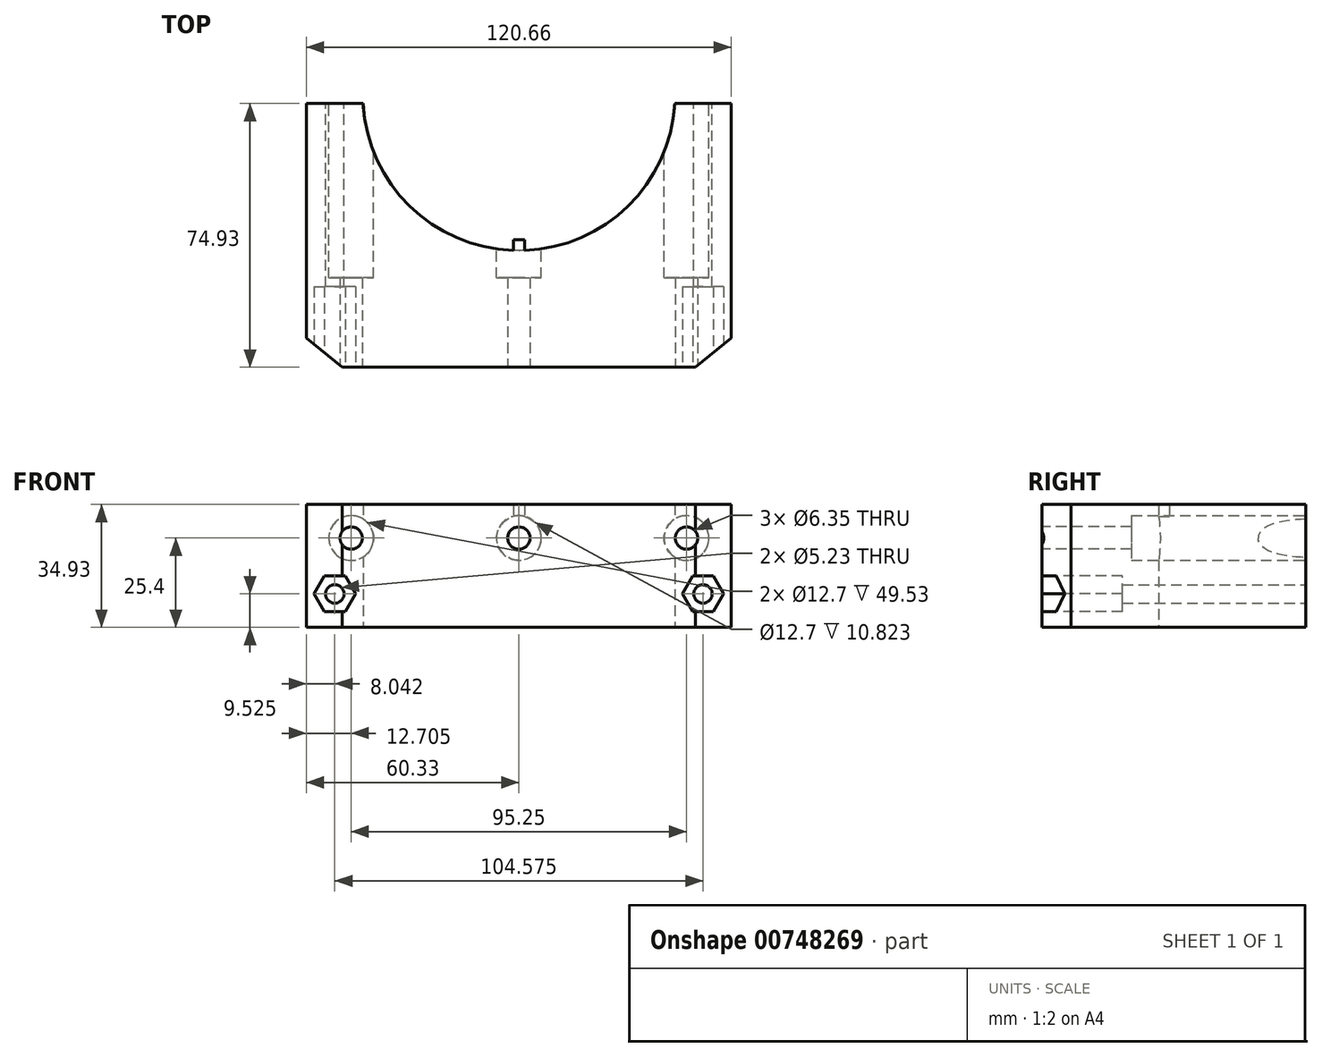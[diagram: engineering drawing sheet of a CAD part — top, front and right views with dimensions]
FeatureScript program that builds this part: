
annotation { "Feature Type Name" : "Feature", "Feature Type Description" : "" }
export const myFeature = defineFeature(function(context is Context, id is Id, definition is map)
    precondition{}
    {
        {
            var Q0;
            Q0=qCreatedBy(makeId("Top.planeOp"),FACE);
            var sketch = newSketch(context, id + "F0", { "sketchPlane" : qUnion([Q0])});
            skCircle(sketch, "E0", {"center": v(0, 0) * mm, "radius": 44.32 * mm, "construction": true});
            skLineSegment(sketch, "E1.bottom", {"start": v(60.32, -77.47) * mm, "end": v(-60.33, -77.47) * mm, "construction": true});
            skLineSegment(sketch, "E1.top", {"start": v(60.33, 77.47) * mm, "end": v(-60.32, 77.47) * mm, "construction": true});
            skLineSegment(sketch, "E1.left", {"start": v(60.33, -77.47) * mm, "end": v(60.33, 77.47) * mm, "construction": true});
            skLineSegment(sketch, "E1.right", {"start": v(-60.33, -77.47) * mm, "end": v(-60.32, 77.47) * mm, "construction": true});
            skLineSegment(sketch, "E2", {"start": v(-60.33, 0) * mm, "end": v(60.32, 0) * mm, "construction": true});
            skLineSegment(sketch, "E3.0", {"start": v(-60.33, -2.54) * mm, "end": v(60.32, -2.54) * mm, "construction": true});
            skLineSegment(sketch, "E4", {"start": v(-44.25, -2.54) * mm, "end": v(-60.33, -2.54) * mm});
            skLineSegment(sketch, "E5", {"start": v(-60.33, -2.54) * mm, "end": v(-60.33, -69.19) * mm});
            skLineSegment(sketch, "E6", {"start": v(-50.17, -77.47) * mm, "end": v(50.16, -77.47) * mm});
            skLineSegment(sketch, "E7", {"start": v(60.32, -69.19) * mm, "end": v(60.32, -2.54) * mm});
            skLineSegment(sketch, "E8", {"start": v(60.32, -2.54) * mm, "end": v(44.25, -2.54) * mm});
            skLineSegment(sketch, "E9", {"start": v(0, -44.32) * mm, "end": v(0, -77.47) * mm, "construction": true});
            skLineSegment(sketch, "E10.0", {"start": v(-1.59, -43.72) * mm, "end": v(-1.59, -60.32) * mm, "construction": true});
            skLineSegment(sketch, "E11.0", {"start": v(1.59, -43.93) * mm, "end": v(1.59, -60.33) * mm, "construction": true});
            skArc(sketch, "E12", {"start": v(1.59, -44.3) * mm, "mid": v(31, -31.68) * mm, "end": v(44.25, -2.54) * mm});
            skArc(sketch, "E13", {"start": v(-44.25, -2.54) * mm, "mid": v(-31, -31.68) * mm, "end": v(-1.59, -44.3) * mm});
            skLineSegment(sketch, "E14", {"start": v(-1.59, -44.3) * mm, "end": v(-1.59, -41.25) * mm});
            skLineSegment(sketch, "E15", {"start": v(1.59, -44.3) * mm, "end": v(1.59, -41.25) * mm});
            skLineSegment(sketch, "E16", {"start": v(-1.59, -41.25) * mm, "end": v(1.59, -41.25) * mm});
            skLineSegment(sketch, "E17.0", {"start": v(-50.17, -2.54) * mm, "end": v(-50.17, -77.47) * mm, "construction": true});
            skLineSegment(sketch, "E18.0", {"start": v(50.16, -77.47) * mm, "end": v(50.16, -2.54) * mm, "construction": true});
            skLineSegment(sketch, "E19.0", {"start": v(-60.33, -69.19) * mm, "end": v(60.32, -69.19) * mm, "construction": true});
            skLineSegment(sketch, "E20", {"start": v(-60.33, -69.19) * mm, "end": v(-50.17, -77.47) * mm});
            skLineSegment(sketch, "E21", {"start": v(60.32, -69.19) * mm, "end": v(50.16, -77.47) * mm});
            skSolve(sketch);
        }
        {
            var Q0;
            Q0 = qSketchRegion(id + "F0", true);
            extrude(context, id + "F1", {"entities" : qUnion([Q0]), "depth" : 34.92 * mm, "offsetDistance" : 25.4 * mm});
        }
        {
            var Q0;
            Q0=makeQuery(id+"F1.opExtrude","SWEPT_FACE",FACE,{"disambiguationData":[OSD([sQuery(id+"F0.wireOp",EDGE,"E8")])]});
            var sketch = newSketch(context, id + "F2", { "sketchPlane" : qUnion([Q0])});
            skLineSegment(sketch, "E22", {"start": v(-52.29, 34.93) * mm, "end": v(-52.29, 0) * mm, "construction": true});
            skLineSegment(sketch, "E23", {"start": v(-60.32, 9.53) * mm, "end": v(-44.25, 9.53) * mm, "construction": true});
            skCircle(sketch, "E24", {"center": v(-52.29, 9.53) * mm, "radius": 2.62 * mm});
            skSolve(sketch);
        }
        {
            var Q0;
            Q0 = qSketchRegion(id + "F2", true);
            extrude(context, id + "F3", {"entities" : qUnion([Q0]), "operationType" : NewBodyOperationType.REMOVE, "endBound" : BoundingType.THROUGH_ALL, "oppositeDirection" : true, "depth" : 25.4 * mm, "offsetDistance" : 25.4 * mm});
        }
        {
            var Q0;
            Q0=makeQuery(id+"F1.opExtrude","SWEPT_FACE",FACE,{"disambiguationData":[OSD([sQuery(id+"F0.wireOp",EDGE,"E4")])]});
            var sketch = newSketch(context, id + "F4", { "sketchPlane" : qUnion([Q0])});
            skLineSegment(sketch, "E25", {"start": v(52.29, 34.93) * mm, "end": v(52.29, 0) * mm, "construction": true});
            skLineSegment(sketch, "E26", {"start": v(44.25, 9.53) * mm, "end": v(60.33, 9.53) * mm, "construction": true});
            skCircle(sketch, "E27", {"center": v(52.29, 9.53) * mm, "radius": 2.62 * mm});
            skSolve(sketch);
        }
        {
            var Q0;
            Q0 = qSketchRegion(id + "F4", true);
            extrude(context, id + "F5", {"entities" : qUnion([Q0]), "operationType" : NewBodyOperationType.REMOVE, "endBound" : BoundingType.THROUGH_ALL, "oppositeDirection" : true, "depth" : 25.4 * mm, "offsetDistance" : 25.4 * mm});
        }
        {
            var Q0;
            Q0=makeQuery(id+"F1.opExtrude","SWEPT_FACE",FACE,{"disambiguationData":[OSD([sQuery(id+"F0.wireOp",EDGE,"E6")])]});
            var sketch = newSketch(context, id + "F6", { "sketchPlane" : qUnion([Q0])});
            skLineSegment(sketch, "E28", {"start": v(-60.33, 25.4) * mm, "end": v(60.33, 25.4) * mm, "construction": true});
            skCircle(sketch, "E29", {"center": v(-47.63, 25.4) * mm, "radius": 3.18 * mm});
            skCircle(sketch, "E30", {"center": v(47.63, 25.4) * mm, "radius": 3.18 * mm});
            skCircle(sketch, "E31", {"center": v(0, 25.4) * mm, "radius": 3.18 * mm});
            skLineSegment(sketch, "E32", {"start": v(0, 0) * mm, "end": v(0, 34.93) * mm, "construction": true});
            skSolve(sketch);
        }
        {
            var Q0;
            Q0 = qSketchRegion(id + "F6", true);
            extrude(context, id + "F7", {"entities" : qUnion([Q0]), "operationType" : NewBodyOperationType.REMOVE, "endBound" : BoundingType.THROUGH_ALL, "oppositeDirection" : true, "depth" : 25.4 * mm, "offsetDistance" : 25.4 * mm});
        }
        {
            var Q0;
            Q0=makeQuery(id+"F1.opExtrude","SWEPT_FACE",FACE,{"disambiguationData":[OSD([sQuery(id+"F0.wireOp",EDGE,"E8")])]});
            var sketch = newSketch(context, id + "F8", { "sketchPlane" : qUnion([Q0])});
            skCircle(sketch, "E33", {"center": v(-47.63, 25.4) * mm, "radius": 6.35 * mm});
            skLineSegment(sketch, "E34", {"start": v(-47.63, 25.4) * mm, "end": v(47.63, 25.4) * mm, "construction": true});
            skCircle(sketch, "E35", {"center": v(0, 25.4) * mm, "radius": 6.35 * mm});
            skCircle(sketch, "E36", {"center": v(47.63, 25.4) * mm, "radius": 6.35 * mm});
            skSolve(sketch);
        }
        {
            var Q0;
            Q0 = qSketchRegion(id + "F8", true);
            extrude(context, id + "F9", {"entities" : qUnion([Q0]), "operationType" : NewBodyOperationType.REMOVE, "oppositeDirection" : true, "depth" : 49.53 * mm, "offsetDistance" : 25.4 * mm});
        }
        {
            var Q0;
            Q0=makeQuery(id+"F1.opExtrude","SWEPT_FACE",FACE,{"disambiguationData":[OSD([sQuery(id+"F0.wireOp",EDGE,"E6")])]});
            var sketch = newSketch(context, id + "F10", { "sketchPlane" : qUnion([Q0])});
            skCircle(sketch, "E37.cCircle", {"center": v(-52.29, 9.53) * mm, "radius": 5.08 * mm, "construction": true});
            skLineSegment(sketch, "E37.0", {"start": v(-46.42, 9.52) * mm, "end": v(-49.35, 4.45) * mm});
            skLineSegment(sketch, "E37.1", {"start": v(-49.35, 4.45) * mm, "end": v(-55.22, 4.45) * mm});
            skLineSegment(sketch, "E37.2", {"start": v(-55.22, 4.45) * mm, "end": v(-58.15, 9.53) * mm});
            skLineSegment(sketch, "E37.3", {"start": v(-58.15, 9.53) * mm, "end": v(-55.22, 14.6) * mm});
            skLineSegment(sketch, "E37.4", {"start": v(-55.22, 14.6) * mm, "end": v(-49.35, 14.6) * mm});
            skLineSegment(sketch, "E37.5", {"start": v(-49.35, 14.6) * mm, "end": v(-46.42, 9.52) * mm});
            skPoint(sketch, "E37.0.midPoint", {"position": v(-47.89, 6.98) * mm});
            skLineSegment(sketch, "E38", {"start": v(-52.29, 9.53) * mm, "end": v(52.29, 9.53) * mm, "construction": true});
            skCircle(sketch, "E39.cCircle", {"center": v(52.29, 9.53) * mm, "radius": 5.08 * mm, "construction": true});
            skLineSegment(sketch, "E39.0", {"start": v(46.42, 9.53) * mm, "end": v(49.35, 14.6) * mm});
            skLineSegment(sketch, "E39.1", {"start": v(49.35, 14.6) * mm, "end": v(55.22, 14.6) * mm});
            skLineSegment(sketch, "E39.2", {"start": v(55.22, 14.6) * mm, "end": v(58.15, 9.52) * mm});
            skLineSegment(sketch, "E39.3", {"start": v(58.15, 9.53) * mm, "end": v(55.22, 4.45) * mm});
            skLineSegment(sketch, "E39.4", {"start": v(55.22, 4.45) * mm, "end": v(49.35, 4.45) * mm});
            skLineSegment(sketch, "E39.5", {"start": v(49.35, 4.44) * mm, "end": v(46.42, 9.53) * mm});
            skPoint(sketch, "E39.0.midPoint", {"position": v(47.89, 12.07) * mm});
            skLineSegment(sketch, "E40.1", {"start": v(-46.42, 9.53) * mm, "end": v(-49.35, 4.45) * mm});
            skLineSegment(sketch, "E40.3", {"start": v(-55.22, 4.44) * mm, "end": v(-58.15, 9.53) * mm});
            skPoint(sketch, "E40.0.midPoint", {"position": v(-47.89, 12.07) * mm});
            skLineSegment(sketch, "E41.2", {"start": v(49.35, 4.45) * mm, "end": v(46.42, 9.53) * mm});
            skLineSegment(sketch, "E41.5", {"start": v(55.22, 14.6) * mm, "end": v(58.15, 9.53) * mm});
            skPoint(sketch, "E41.0.midPoint", {"position": v(56.69, 6.98) * mm});
            skSolve(sketch);
        }
        {
            var Q0;
            Q0 = qSketchRegion(id + "F10", true);
            extrude(context, id + "F11", {"entities" : qUnion([Q0]), "operationType" : NewBodyOperationType.REMOVE, "oppositeDirection" : true, "depth" : 22.86 * mm, "offsetDistance" : 25.4 * mm});
        }
        {
            var Q0;
            Q0=makeQuery(id+"F1.opExtrude","CAP_FACE",FACE,{"disambiguationData":[OSD([sQuery(id+"F0.wireOp",EDGE,"E4"),sQuery(id+"F0.wireOp",EDGE,"E5"),sQuery(id+"F0.wireOp",EDGE,"E6"),sQuery(id+"F0.wireOp",EDGE,"E7"),sQuery(id+"F0.wireOp",EDGE,"E8"),sQuery(id+"F0.wireOp",EDGE,"E12"),sQuery(id+"F0.wireOp",EDGE,"E13"),sQuery(id+"F0.wireOp",EDGE,"E14"),sQuery(id+"F0.wireOp",EDGE,"E15"),sQuery(id+"F0.wireOp",EDGE,"E16"),sQuery(id+"F0.wireOp",EDGE,"E20"),sQuery(id+"F0.wireOp",EDGE,"E21")])],"isStart":true});
            var sketch = newSketch(context, id + "F12", { "sketchPlane" : qUnion([Q0])});
            skCircle(sketch, "E42", {"center": v(0, 0) * mm, "radius": 44.32 * mm, "construction": true});
            skLineSegment(sketch, "E43", {"start": v(1.59, 44.3) * mm, "end": v(1.59, 41.25) * mm});
            skLineSegment(sketch, "E44", {"start": v(1.59, 41.25) * mm, "end": v(-1.59, 41.25) * mm});
            skLineSegment(sketch, "E45", {"start": v(-1.59, 41.25) * mm, "end": v(-1.59, 44.3) * mm});
            skArc(sketch, "E46", {"start": v(-1.59, 44.3) * mm, "mid": v(0, 44.32) * mm, "end": v(1.59, 44.3) * mm});
            skSolve(sketch);
        }
        {
            var Q0;
            Q0 = qSketchRegion(id + "F12", true);
            extrude(context, id + "F13", {"entities" : qUnion([Q0]), "operationType" : NewBodyOperationType.REMOVE, "oppositeDirection" : true, "depth" : 25.4 * mm, "offsetDistance" : 25.4 * mm});
        }
    });
